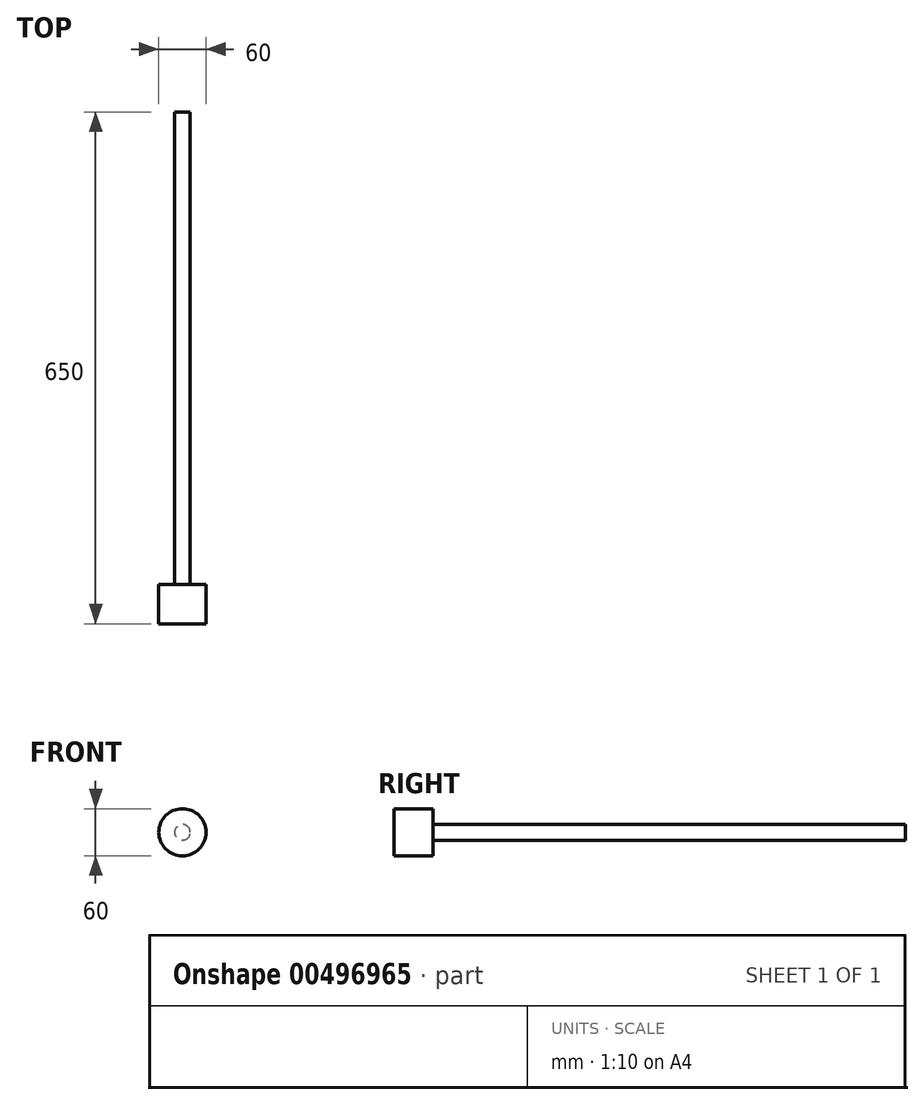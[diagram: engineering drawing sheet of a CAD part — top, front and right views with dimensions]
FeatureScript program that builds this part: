
annotation { "Feature Type Name" : "Feature", "Feature Type Description" : "" }
export const myFeature = defineFeature(function(context is Context, id is Id, definition is map)
    precondition{}
    {
        {
            var Q0;
            Q0=qCreatedBy(makeId("Front.planeOp"),FACE);
            var sketch = newSketch(context, id + "F0", { "sketchPlane" : qUnion([Q0])});
            skCircle(sketch, "E0", {"center": v(0, 0) * mm, "radius": 10 * mm});
            skSolve(sketch);
        }
        {
            var Q0;
            Q0=qSketchRegion(id+"F0",true);
            extrude(context, id + "F1", {"entities" : qUnion([Q0]), "depth" : 600 * mm});
        }
        {
            var Q0;
            Q0=makeQuery(id+"F1.opExtrude","CAP_FACE",FACE,{"disambiguationData":[OSD([sQuery(id+"F0.wireOp",EDGE,"E0")])],"isStart":false});
            var sketch = newSketch(context, id + "F2", { "sketchPlane" : qUnion([Q0])});
            skCircle(sketch, "E1", {"center": v(0, 0) * mm, "radius": 30 * mm});
            skSolve(sketch);
        }
        {
            var Q0;
            Q0=qSketchRegion(id+"F2",true);
            extrude(context, id + "F3", {"entities" : qUnion([Q0]), "depth" : 50 * mm});
        }
    });
